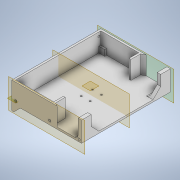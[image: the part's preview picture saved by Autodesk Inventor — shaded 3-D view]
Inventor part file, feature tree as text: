
AUTODESK INVENTOR PART (.ipt)
format: ipt  version: 2020 (Build 240168000, 168)  size: 317,440 bytes
history: native  units: mm
features: sketch x9, extrude x6, plane x6, rib x3, fillet x2, chamfer x1, hole x1, mirror x1
ambient origin geometry x8: Origin, YZ Plane, XZ Plane, XY Plane, X Axis, Y Axis, Z Axis, Center Point
bodies: Solid1 (feature_tree)
feature tree (29):
  extrude  "Extrusion1"  Depth=5.0mm
  extrude  "Extrusion2"  Depth=69.0mm
  extrude  "Extrusion3"  Depth=10.0mm
  extrude  "Extrusion4"  Depth=20.0mm
  chamfer  "Chamfer1"  [1 undecoded]
  fillet  "Fillet1"  Radius=5.0mm
  plane  "Work Plane3"
  plane  "Work Plane2"
  plane  "Work Plane4"
  extrude  "Extrusion8"  Depth=175.0mm TaperAngle=0.0deg
  extrude  "Extrusion9"  Depth=72.0mm
  hole  "Hole1"  [1 undecoded]
  plane  "Work Plane1"
  mirror  "Mirror1"
  plane  "Work Plane5"
  plane  "Work Plane6"
  sketch  "Sketch11"  dims[d23=5.0mm d24=72.0mm]
  sketch  "Sketch12"  dims[d25=5.0mm d33=25.0mm d34=20.594885mm]
  sketch  "Sketch13"  dims[d37=25.0mm d38=9.0mm d39=170.0mm d40=0.0mm d41=20.0mm d42=2.0mm d43=45.0deg d44=8.0mm d54=4.3mm d55=5.5mm d56=6.0mm d57=20.0mm d59=29.0mm d60=20.0mm d62=23.0mm d65=0.0mm d66=0.0mm d67=5.0mm d68=15.0mm d69=15.0mm d70=0.0mm d71=10.0mm d72=10.0mm d73=6.0mm d74=6.0mm d75=5.9mm d76=6.0mm d77=19.05mm d78=4.775mm d79=45.0deg d80=8.0mm d81=0.0mm d82=15.0mm d83=10.0mm d84=10.0mm d88=95.0mm d89=68.0mm d90=45.0deg d91=1.0mm d92=5.0mm d93=0.0mm d94=0.0mm d95=1.0mm d96=1.0mm d97=1.0mm d98=5.0mm d99=0.0mm d100=0.0mm d101=1.0mm d102=1.0mm d103=1.0mm d104=5.0mm d105=0.0mm d106=0.0mm d107=1.0mm d108=1.0mm d109=5.0mm]
  rib  "Rib1"
  rib  "Rib2"
  rib  "Rib3"
  fillet  "Fillet2"  Radius=20.594885mm
  sketch  "Sketch1"  dims[d0=230.0mm d1=5.0mm]
  sketch  "Sketch2"  dims[d2=69.0mm d3=0.0mm d4=5.3mm]
  sketch  "Sketch3"  dims[d5=10.0mm d6=10.0mm]
  sketch  "Sketch4"  dims[d7=20.0mm d9=210.0mm d10=20.0mm d12=49.0mm d15=95.0mm]
  sketch  "Sketch9"  dims[d16=20.0mm d17=0.0mm d18=0.0mm d19=5.0mm]
  sketch  "Sketch10"  dims[d20=7.0mm d21=175.0mm d22=0.0mm]
note: 2 required parameter values undecoded (feature->parameter linkage not recoverable at this tier; creation-order binding heuristic only, values carry confidence <= 0.55)
